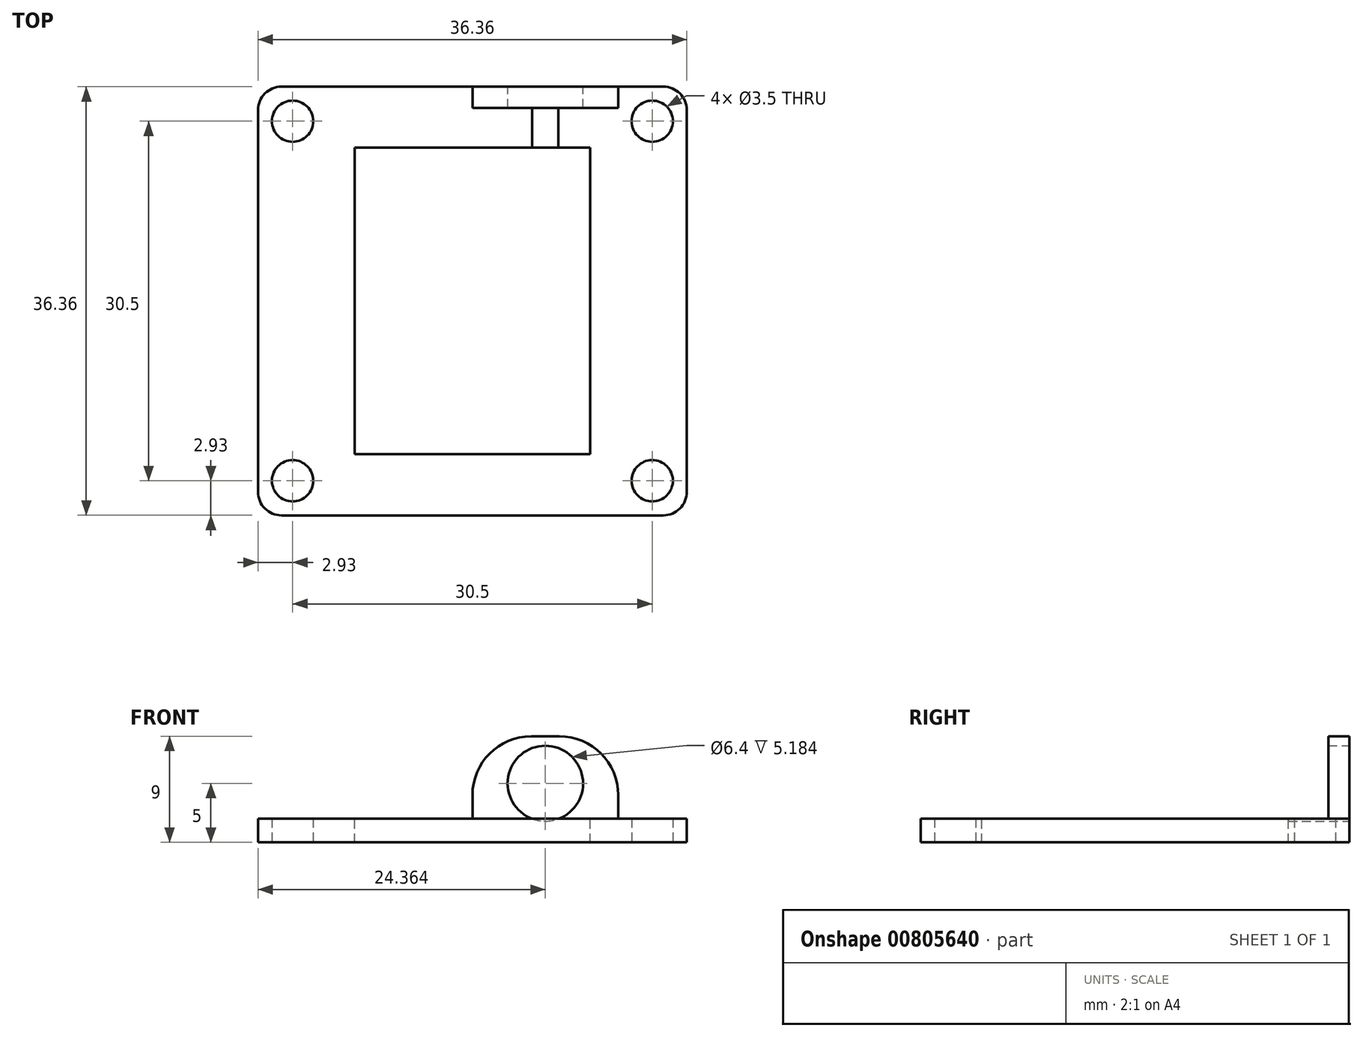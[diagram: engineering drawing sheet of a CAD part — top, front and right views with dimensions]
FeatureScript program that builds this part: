
annotation { "Feature Type Name" : "Feature", "Feature Type Description" : "" }
export const myFeature = defineFeature(function(context is Context, id is Id, definition is map)
    precondition{}
    {
        {
            var Q0;
            Q0=qCreatedBy(makeId("Top.planeOp"),FACE);
            var sketch = newSketch(context, id + "F0", { "sketchPlane" : qUnion([Q0])});
            skLineSegment(sketch, "E0.bottom", {"start": v(-15.25, 15.25) * mm, "end": v(15.25, 15.25) * mm});
            skLineSegment(sketch, "E0.top", {"start": v(-15.25, -15.25) * mm, "end": v(15.25, -15.25) * mm});
            skLineSegment(sketch, "E0.left", {"start": v(-15.25, 15.25) * mm, "end": v(-15.25, -15.25) * mm});
            skLineSegment(sketch, "E0.right", {"start": v(15.25, 15.25) * mm, "end": v(15.25, -15.25) * mm});
            skPoint(sketch, "E0.middle", {"position": v(0, 0) * mm});
            skCircle(sketch, "E1", {"center": v(-15.25, 15.25) * mm, "radius": 1.75 * mm});
            skCircle(sketch, "E2", {"center": v(15.25, 15.25) * mm, "radius": 1.75 * mm});
            skCircle(sketch, "E3", {"center": v(15.25, -15.25) * mm, "radius": 1.75 * mm});
            skCircle(sketch, "E4", {"center": v(-15.25, -15.25) * mm, "radius": 1.75 * mm});
            skLineSegment(sketch, "E5.bottom", {"start": v(-18.18, 18.18) * mm, "end": v(18.18, 18.18) * mm});
            skLineSegment(sketch, "E5.top", {"start": v(-18.18, -18.18) * mm, "end": v(18.18, -18.18) * mm});
            skLineSegment(sketch, "E5.left", {"start": v(-18.18, 18.18) * mm, "end": v(-18.18, -18.18) * mm});
            skLineSegment(sketch, "E5.right", {"start": v(18.18, 18.18) * mm, "end": v(18.18, -18.18) * mm});
            skCircle(sketch, "E6", {"center": v(-15.25, 15.25) * mm, "radius": 2.5 * mm, "construction": true});
            skSolve(sketch);
        }
        {
            var Q0;
            Q0=qSketchRegion(id+"F0",true);
            var Q1;
            {var subQ5=sQuery(id+"F0.wireOp",EDGE,"E1");var subQ13=sQuery(id+"F0.wireOp",EDGE,"E0.bottom");var subQ14=makeQuery(id+"F0.imprint","INTERSECT",VERTEX,{"derivedFrom":[subQ13,subQ5]});Q1=makeQuery(id+"F0.imprint","IMPRINT",FACE,{"disambiguationData":[TD([[makeQuery(id+"F0.imprint","IMPRINT",EDGE,{"disambiguationData":[TD([[subQ14,-1.0]])],"derivedFrom":subQ13}),-1.0]])]});}
            extrude(context, id + "F1", {"entities" : qUnion([Q0, Q1]), "depth" : 2 * mm, "offsetDistance" : 25 * mm});
        }
        {
            var Q0;
            Q0=makeQuery(id+"F1.opExtrude","CAP_FACE",FACE,{"disambiguationData":[OSD([sQuery(id+"F0.wireOp",EDGE,"E1"),sQuery(id+"F0.wireOp",EDGE,"E2"),sQuery(id+"F0.wireOp",EDGE,"E3"),sQuery(id+"F0.wireOp",EDGE,"E4"),sQuery(id+"F0.wireOp",EDGE,"E5.bottom"),sQuery(id+"F0.wireOp",EDGE,"E5.top"),sQuery(id+"F0.wireOp",EDGE,"E5.left"),sQuery(id+"F0.wireOp",EDGE,"E5.right")])],"isStart":false});
            var sketch = newSketch(context, id + "F2", { "sketchPlane" : qUnion([Q0])});
            skLineSegment(sketch, "E7.bottom", {"start": v(-10, 13) * mm, "end": v(10, 13) * mm});
            skLineSegment(sketch, "E7.top", {"start": v(-10, -13) * mm, "end": v(10, -13) * mm});
            skLineSegment(sketch, "E7.left", {"start": v(-10, 13) * mm, "end": v(-10, -13) * mm});
            skLineSegment(sketch, "E7.right", {"start": v(10, 13) * mm, "end": v(10, -13) * mm});
            skPoint(sketch, "E7.middle", {"position": v(0, 0) * mm});
            skSolve(sketch);
        }
        {
            var Q0;
            Q0=qSketchRegion(id+"F2",true);
            extrude(context, id + "F3", {"entities" : qUnion([Q0]), "operationType" : NewBodyOperationType.REMOVE, "oppositeDirection" : true, "depth" : 25 * mm, "offsetDistance" : 25 * mm});
        }
        {
            var Q0;
            Q0=makeQuery(id+"F1.opExtrude","CAP_FACE",FACE,{"disambiguationData":[OSD([sQuery(id+"F0.wireOp",EDGE,"E1"),sQuery(id+"F0.wireOp",EDGE,"E2"),sQuery(id+"F0.wireOp",EDGE,"E3"),sQuery(id+"F0.wireOp",EDGE,"E4"),sQuery(id+"F0.wireOp",EDGE,"E5.bottom"),sQuery(id+"F0.wireOp",EDGE,"E5.top"),sQuery(id+"F0.wireOp",EDGE,"E5.left"),sQuery(id+"F0.wireOp",EDGE,"E5.right")])],"isStart":false});
            var sketch = newSketch(context, id + "F4", { "sketchPlane" : qUnion([Q0])});
            skLineSegment(sketch, "E8.bottom", {"start": v(3.18, 18.18) * mm, "end": v(9.18, 18.18) * mm});
            skLineSegment(sketch, "E8.top", {"start": v(3.18, 16.38) * mm, "end": v(9.18, 16.38) * mm});
            skLineSegment(sketch, "E8.left", {"start": v(3.18, 18.18) * mm, "end": v(3.18, 16.38) * mm});
            skLineSegment(sketch, "E8.right", {"start": v(9.18, 18.18) * mm, "end": v(9.18, 16.38) * mm});
            skPoint(sketch, "E8.middle", {"position": v(6.18, 17.28) * mm});
            skLineSegment(sketch, "E9.bottom", {"start": v(0, 18.18) * mm, "end": v(12.37, 18.18) * mm});
            skLineSegment(sketch, "E9.top", {"start": v(0, 16.38) * mm, "end": v(12.37, 16.38) * mm});
            skLineSegment(sketch, "E9.left", {"start": v(0, 18.18) * mm, "end": v(0, 16.38) * mm});
            skLineSegment(sketch, "E9.right", {"start": v(12.37, 18.18) * mm, "end": v(12.37, 16.38) * mm});
            skSolve(sketch);
        }
        {
            var Q0;
            Q0 = qSketchRegion(id + "F4", true);
            extrude(context, id + "F5", {"entities" : qUnion([Q0]), "operationType" : NewBodyOperationType.ADD, "depth" : 7 * mm, "offsetDistance" : 25 * mm});
        }
        {
            var Q0;
            Q0=makeQuery(id+"F5.boolean.opBoolean","MERGE",FACE,{"derivedFrom":[makeQuery(id+"F1.opExtrude","SWEPT_FACE",FACE,{"disambiguationData":[OSD([sQuery(id+"F0.wireOp",EDGE,"E5.bottom")])]}),makeQuery(id+"F5.opExtrude","SWEPT_FACE",FACE,{"disambiguationData":[OSD([sQuery(id+"F4.wireOp",EDGE,"E9.bottom")])]})]});
            var sketch = newSketch(context, id + "F6", { "sketchPlane" : qUnion([Q0])});
            skCircle(sketch, "E10", {"center": v(-6.18, 5) * mm, "radius": 3.2 * mm});
            skSolve(sketch);
        }
        {
            var Q0;
            Q0 = qSketchRegion(id + "F6", true);
            extrude(context, id + "F7", {"entities" : qUnion([Q0]), "operationType" : NewBodyOperationType.REMOVE, "oppositeDirection" : true, "depth" : 25 * mm, "offsetDistance" : 25 * mm});
        }
        {
            var Q0;
            Q0=makeQuery(id+"F5.opExtrude","CAP_EDGE",EDGE,{"disambiguationData":[OSD([sQuery(id+"F4.wireOp",EDGE,"E9.right")])],"isStart":false});
            var Q1;
            Q1=makeQuery(id+"F5.opExtrude","CAP_EDGE",EDGE,{"disambiguationData":[OSD([sQuery(id+"F4.wireOp",EDGE,"E9.left")])],"isStart":false});
            fillet(context, id + "F8", {"entities" : qUnion([Q0, Q1]), "radius" : 5 * mm, "tangentPropagation" : true, "allowEdgeOverflow" : false});
        }
        {
            var Q0;
            Q0=makeQuery(id+"F1.opExtrude","SWEPT_EDGE",EDGE,{"disambiguationData":[OSD([sQuery(id+"F0.wireOp",EDGE,"E5.bottom"),sQuery(id+"F0.wireOp",EDGE,"E5.left")])]});
            var Q1;
            Q1=makeQuery(id+"F1.opExtrude","SWEPT_EDGE",EDGE,{"disambiguationData":[OSD([sQuery(id+"F0.wireOp",EDGE,"E5.top"),sQuery(id+"F0.wireOp",EDGE,"E5.left")])]});
            var Q2;
            Q2=makeQuery(id+"F1.opExtrude","SWEPT_EDGE",EDGE,{"disambiguationData":[OSD([sQuery(id+"F0.wireOp",EDGE,"E5.bottom"),sQuery(id+"F0.wireOp",EDGE,"E5.right")])]});
            var Q3;
            Q3=makeQuery(id+"F1.opExtrude","SWEPT_EDGE",EDGE,{"disambiguationData":[OSD([sQuery(id+"F0.wireOp",EDGE,"E5.top"),sQuery(id+"F0.wireOp",EDGE,"E5.right")])]});
            fillet(context, id + "F9", {"entities" : qUnion([Q0, Q1, Q2, Q3]), "radius" : 2 * mm, "tangentPropagation" : true, "allowEdgeOverflow" : false});
        }
    });
